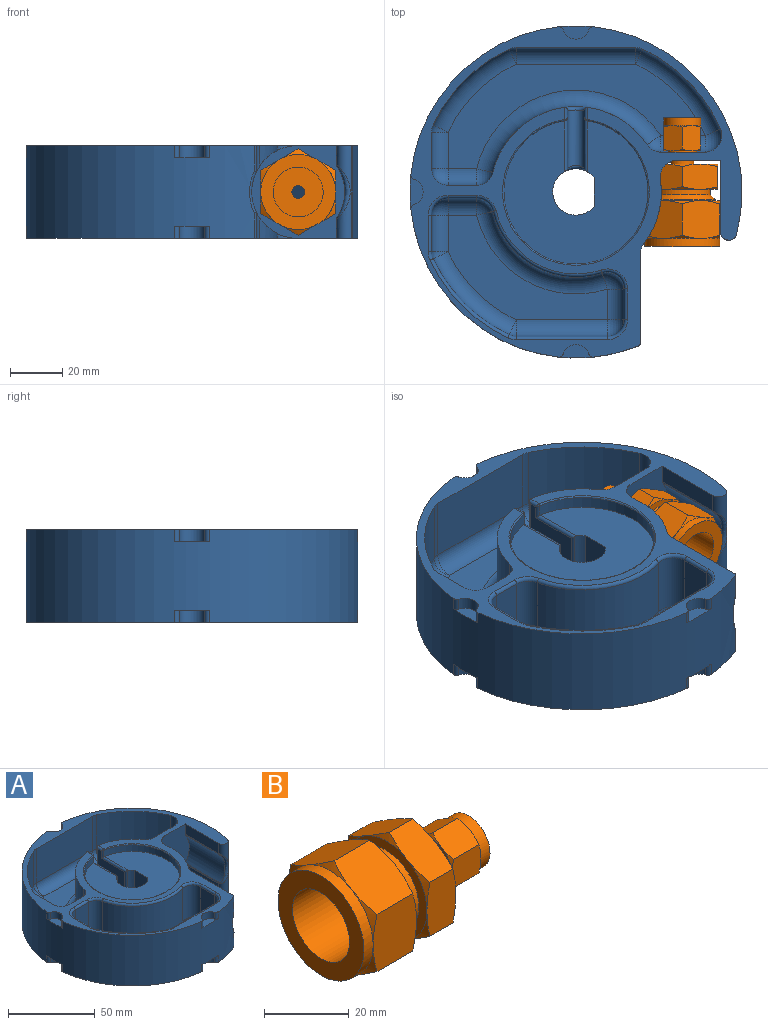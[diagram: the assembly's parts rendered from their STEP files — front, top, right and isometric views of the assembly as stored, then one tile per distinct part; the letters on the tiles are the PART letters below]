
ASSEMBLY  parts=2 mates=1
PART A: 142 faces, bbox 127x127x35.6 mm
  f0: cylinder r=32.64mm len=24.66mm, axis (0,0,-1), area 84.6mm2, adj f1,f4,f18,f19
  f1: cylinder r=17.78mm len=69.72mm, axis (0,-1,0), area 1764.5mm2, adj f0,f2,f7,f8,f17,f18,f19,f20
  f2: cylinder r=6.35mm len=7.28mm, axis (0,0,-1), area 14.1mm2, adj f1,f17,f121,f129
  f3: cylinder r=1.27mm len=20.79mm, axis (0,1,0), area 38.6mm2, adj f69,f87,f88,f90,f105,f132
  f4: plane 126.65x126.31mm, normal (0,0,-1), area 8407.7mm2, adj f0,f9,f15,f16,f17,f18,f19,f20
  f5: cylinder r=6.35mm len=22.86mm, axis (0,0,-1), area 63.5mm2, adj f48,f82,f83,f103
  f6: cylinder r=6.35mm len=22.86mm, axis (0,0,-1), area 273.6mm2, adj f42,f77,f78,f97
  f7: bspline ~16.39x2.56mm, area 25.1mm2, adj f1,f8,f15,f20,f118,f127
  f8: plane 34.27x10.21mm, normal (1,0,0), area 347.7mm2, adj f1,f7,f38,f118,f121
  f9: cylinder r=3.2mm len=35.56mm, axis (0,0,-1), area 181mm2, adj f4,f16,f37,f50,f121,f138
  f10: cylinder r=1.27mm len=34.91mm, axis (-1,0,0), area 69.6mm2, adj f13,f39,f40,f121
  f11: cylinder r=6.35mm len=22.86mm, axis (0,0,1), area 228mm2, adj f13,f40,f77,f95
  f12: cylinder r=1.27mm len=19.52mm, axis (0,0,-1), area 41.5mm2, adj f22,f36,f54,f74,f121
  f13: plane 34.91x22.86mm, normal (0,1,0), area 797.9mm2, adj f10,f11,f76,f94
  f14: plane 25.4x10.92mm, normal (-1,0,0), area 277.4mm2, adj f84,f90,f105
  f15: cylinder r=1.27mm len=10.06mm, axis (0,0,-1), area 12.2mm2, adj f4,f7,f20,f127
  f16: plane 27.31x7.26mm, normal (-1,0,0), area 198.2mm2, adj f4,f9,f17,f51
  f17: plane 35.56x35.56mm, normal (0,-1,0), area 966.3mm2, adj f1,f2,f4,f16,f18,f37,f51,f52
  f18: cylinder r=6.35mm len=7.28mm, axis (0,0,-1), area 14.1mm2, adj f0,f1,f4,f17
  f19: cylinder r=6.35mm len=10.16mm, axis (0,0,-1), area 37.5mm2, adj f0,f1,f4,f20
  f20: plane 34.27x10.21mm, normal (1,0,0), area 347.7mm2, adj f1,f4,f7,f15,f19
  f21: torus R=28.07mm, axis (0,0,1), area 139.1mm2, adj f4,f120
  f22: cylinder r=32.64mm len=58.96mm, axis (0,0,-1), area 1649.5mm2, adj f12,f23,f33,f53,f54,f55,f121
  f23: cylinder r=6.35mm len=24.13mm, axis (0,0,-1), area 150.8mm2, adj f22,f24,f56,f121
  f24: plane 24.13x17mm, normal (0,1,0), area 316.6mm2, adj f23,f57,f121,f122,f135
  f25: cylinder r=60.32mm len=30.52mm, axis (0,0,-1), area 1050.9mm2, adj f26,f59,f121,f122
  f26: cylinder r=6.35mm len=24.13mm, axis (0,0,-1), area 67mm2, adj f25,f27,f60,f121
  f27: plane 45.72x24.13mm, normal (0,-1,0), area 1103.2mm2, adj f26,f28,f61,f121
  f28: cylinder r=6.35mm len=24.13mm, axis (0,0,-1), area 67mm2, adj f27,f29,f62,f121
  f29: cylinder r=60.32mm len=29.08mm, axis (0,0,-1), area 1012.1mm2, adj f28,f30,f63,f121
  f30: cylinder r=6.35mm len=24.13mm, axis (0,0,-1), area 67.1mm2, adj f29,f31,f64,f121
  f31: plane 24.13x14mm, normal (1,0,0), area 337.7mm2, adj f30,f65,f121,f139
  f32: plane 24.13x10.92mm, normal (0,1,0), area 263.6mm2, adj f33,f67,f121,f139
  f33: cylinder r=6.35mm len=24.13mm, axis (0,0,-1), area 205.5mm2, adj f22,f32,f68,f121
  f34: cylinder r=1.27mm len=4.61mm, axis (0,1,0), area 7.7mm2, adj f55,f69,f70,f71,f121
  f35: torus R=28.07mm, axis (0,0,1), area 132.1mm2, adj f71,f72,f121,f132
  f36: cylinder r=1.27mm len=4.61mm, axis (0,-1,0), area 7.7mm2, adj f12,f72,f73,f74,f121
  f37: plane 27.31x7.26mm, normal (-1,0,0), area 198.2mm2, adj f9,f17,f75,f121
  f38: cylinder r=6.35mm len=10.16mm, axis (0,0,-1), area 37.5mm2, adj f1,f8,f121,f129
  f39: torus R=7.62mm, axis (0,0,1), area 5.9mm2, adj f10,f49,f76,f121
  f40: torus R=7.62mm, axis (0,0,1), area 21.3mm2, adj f10,f11,f41,f121
  f41: cylinder r=1.27mm len=11.81mm, axis (0,-1,0), area 23.6mm2, adj f40,f42,f77,f121
  f42: torus R=7.62mm, axis (0,0,1), area 25.6mm2, adj f6,f41,f43,f121
  f43: torus R=31.37mm, axis (0,0,1), area 106.3mm2, adj f42,f44,f78,f121
  f44: torus R=7.62mm, axis (0,0,1), area 18.2mm2, adj f43,f45,f79,f121
  f45: cylinder r=1.27mm len=10.93mm, axis (1,0,0), area 21.8mm2, adj f44,f46,f80,f121
  f46: torus R=7.62mm, axis (0,0,1), area 21.3mm2, adj f45,f47,f81,f121
  f47: cylinder r=1.27mm len=13.99mm, axis (0,1,0), area 27.9mm2, adj f46,f48,f82,f121
  f48: torus R=7.62mm, axis (0,0,1), area 5.9mm2, adj f5,f47,f49,f121
  f49: torus R=61.59mm, axis (0,0,1), area 84.4mm2, adj f39,f48,f83,f121
  f50: bspline ~21.05x5.26mm, area 49.3mm2, adj f9,f51,f52,f75
  f51: cylinder r=1.27mm len=27.31mm, axis (0,-1,0), area 20.3mm2, adj f16,f17,f50,f52
  f52: cylinder r=17.78mm len=27.31mm, axis (0,-1,0), area 568.2mm2, adj f17,f50,f51,f75
  f53: torus R=38.99mm, axis (0,0,1), area 810.3mm2, adj f22,f56,f68,f85
  f54: bspline ~9.25x4.45mm, area 24.1mm2, adj f12,f22,f55,f86
  f55: cylinder r=1.27mm len=19.52mm, axis (0,0,-1), area 41.5mm2, adj f22,f34,f54,f69,f121
  f56: sphere r=6.35mm, area 28.7mm2, adj f23,f53,f57
  f57: cylinder r=6.35mm len=17mm, axis (-1,0,0), area 169.6mm2, adj f24,f56,f58,f85
  f58: sphere r=6.35mm, area 79.9mm2, adj f57,f59,f122
  f59: torus R=53.98mm, axis (0,0,1), area 417.8mm2, adj f25,f58,f60,f85
  f60: sphere r=6.35mm, area 13.6mm2, adj f26,f59,f61
  f61: cylinder r=6.35mm len=45.72mm, axis (1,0,0), area 456mm2, adj f27,f60,f62,f85
  f62: sphere r=6.35mm, area 13.6mm2, adj f28,f61,f63
  f63: torus R=53.98mm, axis (0,0,1), area 402.4mm2, adj f29,f62,f64,f85
  f64: sphere r=6.35mm, area 17.7mm2, adj f30,f63,f65
  f65: cylinder r=6.35mm len=14mm, axis (0,1,0), area 139.6mm2, adj f31,f64,f66,f85
  f66: sphere r=6.35mm, area 63.4mm2, adj f65,f67,f139
  f67: cylinder r=6.35mm len=10.92mm, axis (-1,0,0), area 108.9mm2, adj f32,f66,f68,f85
  f68: sphere r=6.35mm, area 36.5mm2, adj f33,f53,f67
  f69: plane 21.92x18.25mm, normal (1,0,0), area 301.7mm2, adj f3,f34,f55,f86,f87,f88
  f70: bspline ~1.26x1.26mm, area 0.6mm2, adj f34,f71,f88
  f71: bspline ~0.52x0.52mm, area 0.1mm2, adj f34,f35,f70,f132
  f72: bspline ~0.52x0.52mm, area 0.1mm2, adj f35,f36,f73,f132
  f73: bspline ~1.26x1.26mm, area 0.6mm2, adj f36,f72,f89
  f74: plane 21.92x18.25mm, normal (-1,0,0), area 301.7mm2, adj f12,f36,f86,f89,f91,f92
  f75: cylinder r=1.27mm len=27.31mm, axis (0,-1,0), area 20.3mm2, adj f17,f37,f50,f52
  f76: cylinder r=6.35mm len=22.86mm, axis (0,0,-1), area 63.5mm2, adj f13,f39,f83,f93
  f77: plane 22.86x11.81mm, normal (-1,0,0), area 270.1mm2, adj f6,f11,f41,f96
  f78: cylinder r=32.64mm len=41.86mm, axis (0,0,-1), area 1234.9mm2, adj f6,f43,f79,f98
  f79: cylinder r=6.35mm len=22.86mm, axis (0,0,-1), area 194.6mm2, adj f44,f78,f80,f99
  f80: plane 22.86x10.93mm, normal (0,-1,0), area 249.7mm2, adj f45,f79,f81,f100
  f81: cylinder r=6.35mm len=22.86mm, axis (0,0,-1), area 228mm2, adj f46,f80,f82,f101
  f82: plane 22.86x13.98mm, normal (1,0,0), area 319.7mm2, adj f5,f47,f81,f102
  f83: cylinder r=60.32mm len=29.1mm, axis (0,0,-1), area 959.9mm2, adj f5,f49,f76,f104
  f84: plane 55.12x55.12mm, normal (0,0,-1), area 2151.7mm2, adj f14,f105,f120
  f85: plane 98.35x40mm, normal (0,0,1), area 1525.5mm2, adj f53,f57,f59,f61,f63,f65,f67
  f86: cylinder r=3.17mm len=21.92mm, axis (0,-1,0), area 218.6mm2, adj f54,f69,f74,f106
  f87: cylinder r=1.27mm len=14.31mm, axis (0,0,-1), area 19.5mm2, adj f3,f69,f105,f106
  f88: cylinder r=1.27mm len=5.83mm, axis (0,0,-1), area 8.7mm2, adj f3,f69,f70,f132
  f89: cylinder r=1.27mm len=5.83mm, axis (0,0,-1), area 8.7mm2, adj f73,f74,f92,f132
  f90: plane 55.12x54.76mm, normal (0,0,1), area 1983.4mm2, adj f3,f14,f92,f105,f132
  f91: cylinder r=1.27mm len=14.31mm, axis (0,0,-1), area 19.5mm2, adj f74,f92,f105,f106
  f92: cylinder r=1.27mm len=20.79mm, axis (0,-1,0), area 38.6mm2, adj f74,f89,f90,f91,f105,f132
  f93: sphere r=6.35mm, area 13.6mm2, adj f76,f94,f104
  f94: cylinder r=6.35mm len=34.91mm, axis (-1,0,0), area 348.2mm2, adj f13,f93,f95,f107
  f95: sphere r=6.35mm, area 63.3mm2, adj f11,f94,f96
  f96: cylinder r=6.35mm len=11.81mm, axis (0,-1,0), area 117.8mm2, adj f77,f95,f97,f107
  f97: sphere r=6.35mm, area 41.8mm2, adj f6,f96,f98
  f98: torus R=38.99mm, axis (0,0,1), area 576.9mm2, adj f78,f97,f99,f107
  f99: sphere r=6.35mm, area 36.5mm2, adj f79,f98,f100
  f100: cylinder r=6.35mm len=10.93mm, axis (1,0,0), area 109mm2, adj f80,f99,f101,f107
  f101: sphere r=6.35mm, area 40.3mm2, adj f81,f100,f102
  f102: cylinder r=6.35mm len=13.99mm, axis (0,1,0), area 139.5mm2, adj f82,f101,f103,f107
  f103: sphere r=6.35mm, area 17.7mm2, adj f5,f102,f104
  f104: torus R=53.98mm, axis (0,0,1), area 402.8mm2, adj f83,f93,f103,f107
  f105: cylinder r=8.89mm len=25.4mm, axis (0,0,-1), area 975.9mm2, adj f3,f14,f84,f87,f90,f91,f92,f106
  f106: bspline ~7.78x4.45mm, area 19.1mm2, adj f86,f87,f91,f105
  f107: plane 60.94x40.02mm, normal (0,0,1), area 973.7mm2, adj f94,f96,f98,f100,f102,f104
  f108: cylinder r=1.78mm len=4.78mm, axis (0,0,-1), area 11.6mm2, adj f4,f123,f127,f130
  f109: cylinder r=1.78mm len=4.78mm, axis (0,0,1), area 11.6mm2, adj f4,f123,f127,f130
  f110: cylinder r=1.78mm len=4.78mm, axis (0,0,-1), area 11.6mm2, adj f119,f121,f125,f127
  f111: cylinder r=1.78mm len=4.78mm, axis (0,0,1), area 11.6mm2, adj f119,f121,f125,f127
  f112: cylinder r=1.78mm len=4.78mm, axis (0,0,-1), area 11.6mm2, adj f4,f127,f136,f141
  f113: cylinder r=1.78mm len=4.78mm, axis (0,0,-1), area 11.6mm2, adj f121,f124,f127,f140
  f114: cylinder r=1.78mm len=4.78mm, axis (0,0,1), area 11.6mm2, adj f4,f127,f131,f133
  f115: cylinder r=1.78mm len=4.78mm, axis (0,0,-1), area 11.6mm2, adj f4,f127,f131,f133
  f116: cylinder r=1.78mm len=4.78mm, axis (0,0,1), area 11.6mm2, adj f121,f127,f134,f137
  f117: cylinder r=1.78mm len=4.78mm, axis (0,0,-1), area 11.6mm2, adj f121,f127,f134,f137
  f118: cylinder r=1.27mm len=10.06mm, axis (0,0,-1), area 12.2mm2, adj f7,f8,f121,f127
  f119: plane 13.42x5.08mm, normal (0,0,1), area 40.8mm2, adj f110,f111,f125,f127
  f120: cylinder r=27.56mm len=55.12mm, axis (0,0,-1), area 791.7mm2, adj f21,f84
  f121: plane 126.66x126.31mm, normal (0,0,1), area 2617mm2, adj f2,f8,f9,f10,f12,f17,f22,f23
  f122: cylinder r=6.35mm len=24.13mm, axis (0,0,-1), area 303.7mm2, adj f24,f25,f58,f121
  f123: cylinder r=5.08mm len=9.66mm, axis (0,0,-1), area 60.9mm2, adj f4,f108,f109,f130
  f124: plane 13.42x5.08mm, normal (0,0,1), area 40.8mm2, adj f113,f127,f128,f140
  f125: cylinder r=5.08mm len=9.66mm, axis (0,0,-1), area 60.9mm2, adj f110,f111,f119,f121
  f126: cylinder r=1.78mm len=4.78mm, axis (0,0,1), area 11.6mm2, adj f4,f127,f136,f141
  f127: cylinder r=63.5mm len=127mm, axis (0,0,-1), area 11674.8mm2, adj f4,f7,f15,f108,f109,f110,f111,f112
  f128: cylinder r=1.78mm len=4.78mm, axis (0,0,1), area 11.6mm2, adj f121,f124,f127,f140
  f129: cylinder r=32.64mm len=24.66mm, axis (0,0,-1), area 84.6mm2, adj f1,f2,f38,f121
  f130: plane 13.42x5.08mm, normal (0,0,-1), area 40.8mm2, adj f108,f109,f123,f127
  f131: plane 13.42x5.08mm, normal (0,0,-1), area 40.8mm2, adj f114,f115,f127,f133
  f132: cylinder r=27.56mm len=55.12mm, axis (0,0,-1), area 752.7mm2, adj f3,f35,f71,f72,f88,f89,f90,f92
  f133: cylinder r=5.08mm len=9.66mm, axis (0,0,-1), area 60.9mm2, adj f4,f114,f115,f131
  f134: plane 13.42x5.08mm, normal (0,0,1), area 40.8mm2, adj f116,f117,f127,f137
  f135: cylinder r=5.46mm len=10.92mm, axis (0,-1,0), area 108.9mm2, adj f17,f24
  f136: cylinder r=5.08mm len=9.66mm, axis (0,0,-1), area 60.9mm2, adj f4,f112,f126,f141
  f137: cylinder r=5.08mm len=9.66mm, axis (0,0,-1), area 60.9mm2, adj f116,f117,f121,f134
  f138: cylinder r=12.7mm len=35.56mm, axis (0,0,-1), area 37.7mm2, adj f4,f9,f121,f127
  f139: cylinder r=6.35mm len=24.13mm, axis (0,0,1), area 240.7mm2, adj f31,f32,f66,f121
  f140: cylinder r=5.08mm len=9.66mm, axis (0,0,-1), area 60.9mm2, adj f113,f121,f124,f128
  f141: plane 13.42x5.08mm, normal (0,0,-1), area 40.8mm2, adj f112,f126,f127,f136
PART B: 73 faces, bbox 49.3x33.1x33.1 mm
  f0: cone r=15.46mm half-angle=60deg, axis (-1,0,0), area 12.8mm2, adj f7,f27,f39
  f1: plane 6.35x6.35mm, normal (1,0,0), area 13.4mm2, adj f40,f44
  f2: cone r=15.46mm half-angle=60deg, axis (-1,0,0), area 12.8mm2, adj f6,f7,f39
  f3: cone r=15.46mm half-angle=60deg, axis (-1,0,0), area 12.8mm2, adj f7,f19,f27
  f4: plane 28.7x28.7mm, normal (-1,0,0), area 362mm2, adj f5,f37
  f5: cylinder r=14.35mm len=28.7mm, axis (-1,0,0), area 274.8mm2, adj f4,f30,f31,f32,f33,f35,f36
  f6: plane 16.57x14.48mm, normal (0,-1,0), area 225.3mm2, adj f2,f30,f31,f38,f39,f43
  f7: plane 28.7x28.7mm, normal (1,0,0), area 140.3mm2, adj f0,f2,f3,f41,f42,f43,f72
  f8: plane 13.49x9.65mm, normal (0,0.5,0.87), area 140mm2, adj f20,f22,f24,f26,f58,f59
  f9: plane 13.49x9.65mm, normal (0,-0.5,-0.87), area 140mm2, adj f13,f15,f47,f48,f54,f56
  f10: cylinder r=5.56mm len=11.11mm, axis (1,0,0), area 51mm2, adj f16,f46
  f11: plane 26.99x26.99mm, normal (-1,0,0), area 204.9mm2, adj f17,f54,f55,f56,f57,f58,f59
  f12: plane 9.65x7.11mm, normal (0,-0.5,0.87), area 75.7mm2, adj f21,f53,f60,f64,f65,f66
  f13: plane 13.49x9.65mm, normal (0,0.5,-0.87), area 140mm2, adj f9,f23,f26,f48,f56,f57
  f14: plane 14.48x14.35mm, normal (0,0.5,-0.87), area 225.3mm2, adj f19,f32,f36,f38,f41,f42
  f15: plane 15.58x9.65mm, normal (0,-1,0), area 140mm2, adj f9,f20,f25,f47,f54,f55
  f16: plane 14.22x14.22mm, normal (-1,0,0), area 61.9mm2, adj f10,f21,f49,f50,f51,f52,f53
  f17: cylinder r=10.81mm len=21.62mm, axis (-1,0,0), area 146.6mm2, adj f11,f70
  f18: cylinder r=7.11mm len=14.22mm, axis (1,0,0), area 136.2mm2, adj f29,f65,f66,f67,f68,f69,f71
  f19: plane 16.57x14.48mm, normal (0,1,0), area 225.3mm2, adj f3,f14,f27,f33,f36,f41
  f20: plane 13.49x9.65mm, normal (0,-0.5,0.87), area 140mm2, adj f8,f15,f24,f25,f55,f59
  f21: cone r=7.66mm half-angle=60deg, axis (1,0,0), area 3.1mm2, adj f12,f16,f60
  f22: cone r=14.54mm half-angle=65deg, axis (-1,0,0), area 10.8mm2, adj f8,f26,f28
  f23: cone r=14.54mm half-angle=65deg, axis (-1,0,0), area 10.8mm2, adj f13,f26,f28
  f24: cone r=14.54mm half-angle=65deg, axis (-1,0,0), area 10.8mm2, adj f8,f20,f28
  f25: cone r=14.54mm half-angle=65deg, axis (-1,0,0), area 10.8mm2, adj f15,f20,f28
  f26: plane 15.58x9.65mm, normal (0,1,0), area 140mm2, adj f8,f13,f22,f23,f57,f58
  f27: plane 14.48x14.35mm, normal (0,0.5,0.87), area 225.3mm2, adj f0,f3,f19,f33,f35,f39
  f28: plane 26.99x26.99mm, normal (1,0,0), area 509.1mm2, adj f22,f23,f24,f25,f45,f47,f48
  f29: cone r=7.66mm half-angle=60deg, axis (-1,0,0), area 3.1mm2, adj f18,f60,f61
  f30: cone r=15.46mm half-angle=60deg, axis (1,0,0), area 12.8mm2, adj f5,f6,f38
  f31: cone r=15.46mm half-angle=60deg, axis (1,0,0), area 12.8mm2, adj f5,f6,f39
  f32: cone r=15.46mm half-angle=60deg, axis (1,0,0), area 12.8mm2, adj f5,f14,f38
  f33: cone r=15.46mm half-angle=60deg, axis (1,0,0), area 12.8mm2, adj f5,f19,f27
  f34: plane 19.05x19.05mm, normal (-1,0,0), area 266.7mm2, adj f37,f40
  f35: cone r=15.46mm half-angle=60deg, axis (1,0,0), area 12.8mm2, adj f5,f27,f39
  f36: cone r=15.46mm half-angle=60deg, axis (1,0,0), area 12.8mm2, adj f5,f14,f19
  f37: cylinder r=9.53mm len=24.38mm, axis (-1,0,0), area 1459.3mm2, adj f4,f34
  f38: plane 14.48x14.35mm, normal (0,-0.5,-0.87), area 225.3mm2, adj f6,f14,f30,f32,f42,f43
  f39: plane 14.48x14.35mm, normal (0,-0.5,0.87), area 225.3mm2, adj f0,f2,f6,f27,f31,f35
  f40: cylinder r=2.41mm len=9.65mm, axis (-1,0,0), area 146.3mm2, adj f1,f34
  f41: cone r=15.46mm half-angle=60deg, axis (-1,0,0), area 12.8mm2, adj f7,f14,f19
  f42: cone r=15.46mm half-angle=60deg, axis (-1,0,0), area 12.8mm2, adj f7,f14,f38
  f43: cone r=15.46mm half-angle=60deg, axis (-1,0,0), area 12.8mm2, adj f6,f7,f38
  f44: cylinder r=3.17mm len=15.24mm, axis (1,0,0), area 304mm2, adj f1,f71
  f45: cylinder r=4.48mm len=8.95mm, axis (1,0,0), area 71.4mm2, adj f28,f46
  f46: cone r=5.02mm half-angle=45deg, axis (1,0,0), area 48.1mm2, adj f10,f45
  f47: cone r=14.54mm half-angle=65deg, axis (-1,0,0), area 10.8mm2, adj f9,f15,f28
  f48: cone r=14.54mm half-angle=65deg, axis (-1,0,0), area 10.8mm2, adj f9,f13,f28
  f49: cone r=7.66mm half-angle=60deg, axis (1,0,0), area 3.1mm2, adj f16,f60,f61
  f50: cone r=7.66mm half-angle=60deg, axis (1,0,0), area 3.1mm2, adj f16,f61,f62
  f51: cone r=7.66mm half-angle=60deg, axis (1,0,0), area 3.1mm2, adj f16,f62,f63
  f52: cone r=7.66mm half-angle=60deg, axis (1,0,0), area 3.1mm2, adj f16,f63,f64
  f53: cone r=7.66mm half-angle=60deg, axis (1,0,0), area 3.1mm2, adj f12,f16,f64
  f54: cone r=14.54mm half-angle=65deg, axis (1,0,0), area 10.8mm2, adj f9,f11,f15
  f55: cone r=14.54mm half-angle=65deg, axis (1,0,0), area 10.8mm2, adj f11,f15,f20
  f56: cone r=14.54mm half-angle=65deg, axis (1,0,0), area 10.8mm2, adj f9,f11,f13
  f57: cone r=14.54mm half-angle=65deg, axis (1,0,0), area 10.8mm2, adj f11,f13,f26
  f58: cone r=14.54mm half-angle=65deg, axis (1,0,0), area 10.8mm2, adj f8,f11,f26
  f59: cone r=14.54mm half-angle=65deg, axis (1,0,0), area 10.8mm2, adj f8,f11,f20
  f60: plane 9.65x7.11mm, normal (0,0.5,0.87), area 75.7mm2, adj f12,f21,f29,f49,f61,f66
  f61: plane 9.65x8.21mm, normal (0,1,0), area 75.7mm2, adj f29,f49,f50,f60,f62,f67
  f62: plane 9.65x7.11mm, normal (0,0.5,-0.87), area 75.7mm2, adj f50,f51,f61,f63,f67,f68
  f63: plane 9.65x7.11mm, normal (0,-0.5,-0.87), area 75.7mm2, adj f51,f52,f62,f64,f68,f69
  f64: plane 9.65x8.21mm, normal (0,-1,0), area 75.7mm2, adj f12,f52,f53,f63,f65,f69
  f65: cone r=7.66mm half-angle=60deg, axis (-1,0,0), area 3.1mm2, adj f12,f18,f64
  f66: cone r=7.66mm half-angle=60deg, axis (-1,0,0), area 3.1mm2, adj f12,f18,f60
  f67: cone r=7.66mm half-angle=60deg, axis (-1,0,0), area 3.1mm2, adj f18,f61,f62
  f68: cone r=7.66mm half-angle=60deg, axis (-1,0,0), area 3.1mm2, adj f18,f62,f63
  f69: cone r=7.66mm half-angle=60deg, axis (-1,0,0), area 3.1mm2, adj f18,f63,f64
  f70: cone r=11.76mm half-angle=45deg, axis (-1,0,0), area 197.4mm2, adj f17,f72
  f71: plane 14.22x14.22mm, normal (1,0,0), area 127.2mm2, adj f18,f44
  f72: cylinder r=12.7mm len=25.4mm, axis (-1,0,0), area 21.5mm2, adj f7,f70
PLACE A at identity
PLACE B rot(axis=(0,0,1),90deg) t=(40.64,-20.83,17.78)mm
MATE fastened B.f0 <-> A.f1  axis (0,1,0) through (40.64,28.45,17.78)mm
